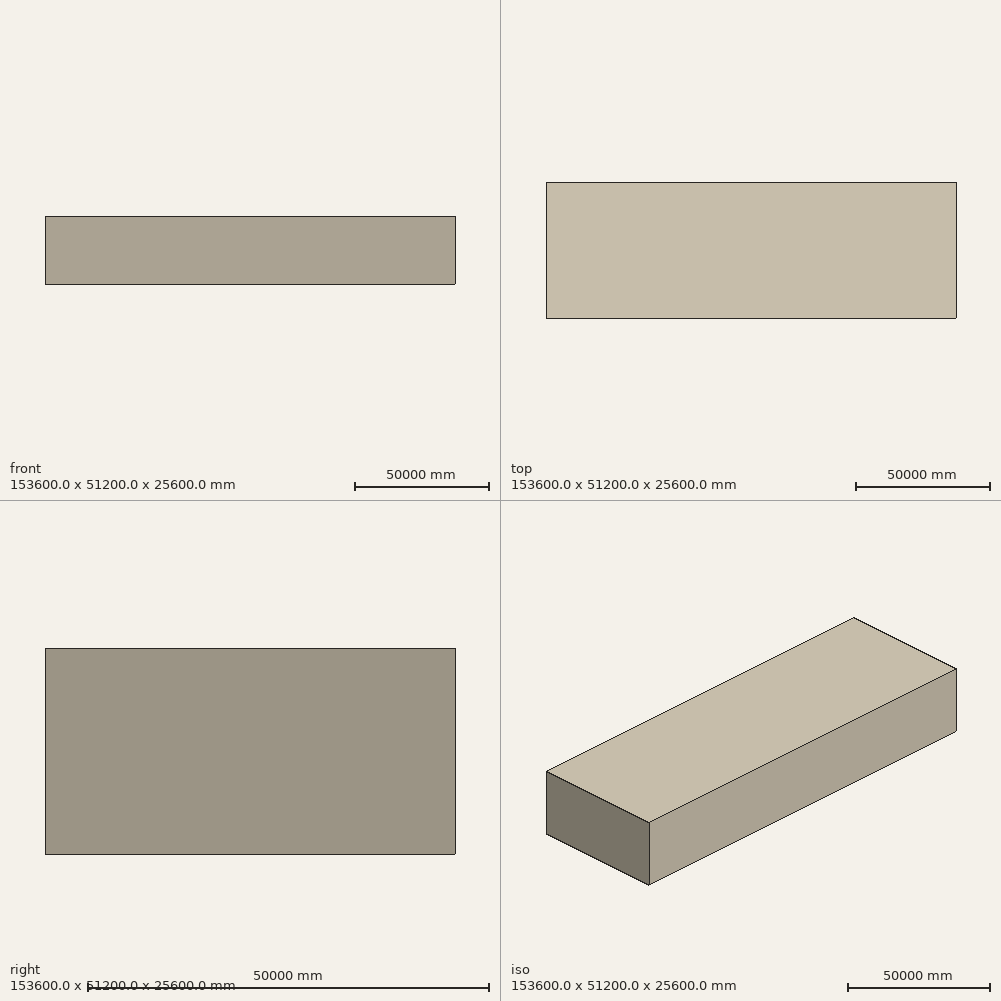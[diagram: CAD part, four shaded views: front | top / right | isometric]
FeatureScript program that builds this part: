
annotation { "Feature Type Name" : "Feature", "Feature Type Description" : "" }
export const myFeature = defineFeature(function(context is Context, id is Id, definition is map)
    precondition{}
    {
        {
            var Q0;
            Q0=qCreatedBy(makeId("Front.planeOp"),FACE);
            var sketch = newSketch(context, id + "F0", { "sketchPlane" : qUnion([Q0])});
            skLineSegment(sketch, "E0.bottom", {"start": v(-51000, 25600) * mm, "end": v(102600, 25600) * mm});
            skLineSegment(sketch, "E0.top", {"start": v(-51000, 0) * mm, "end": v(102600, 0) * mm});
            skLineSegment(sketch, "E0.left", {"start": v(-51000, 25600) * mm, "end": v(-51000, 0) * mm});
            skLineSegment(sketch, "E0.right", {"start": v(102600, 25600) * mm, "end": v(102600, 0) * mm});
            skSolve(sketch);
        }
        {
            var Q0;
            Q0 = qSketchRegion(id + "F0", true);
            extrude(context, id + "F1", {"entities" : qUnion([Q0]), "depth" : 25600 * mm, "hasSecondDirection" : true, "secondDirectionOppositeDirection" : true, "secondDirectionDepth" : 25600 * mm});
        }
    });
